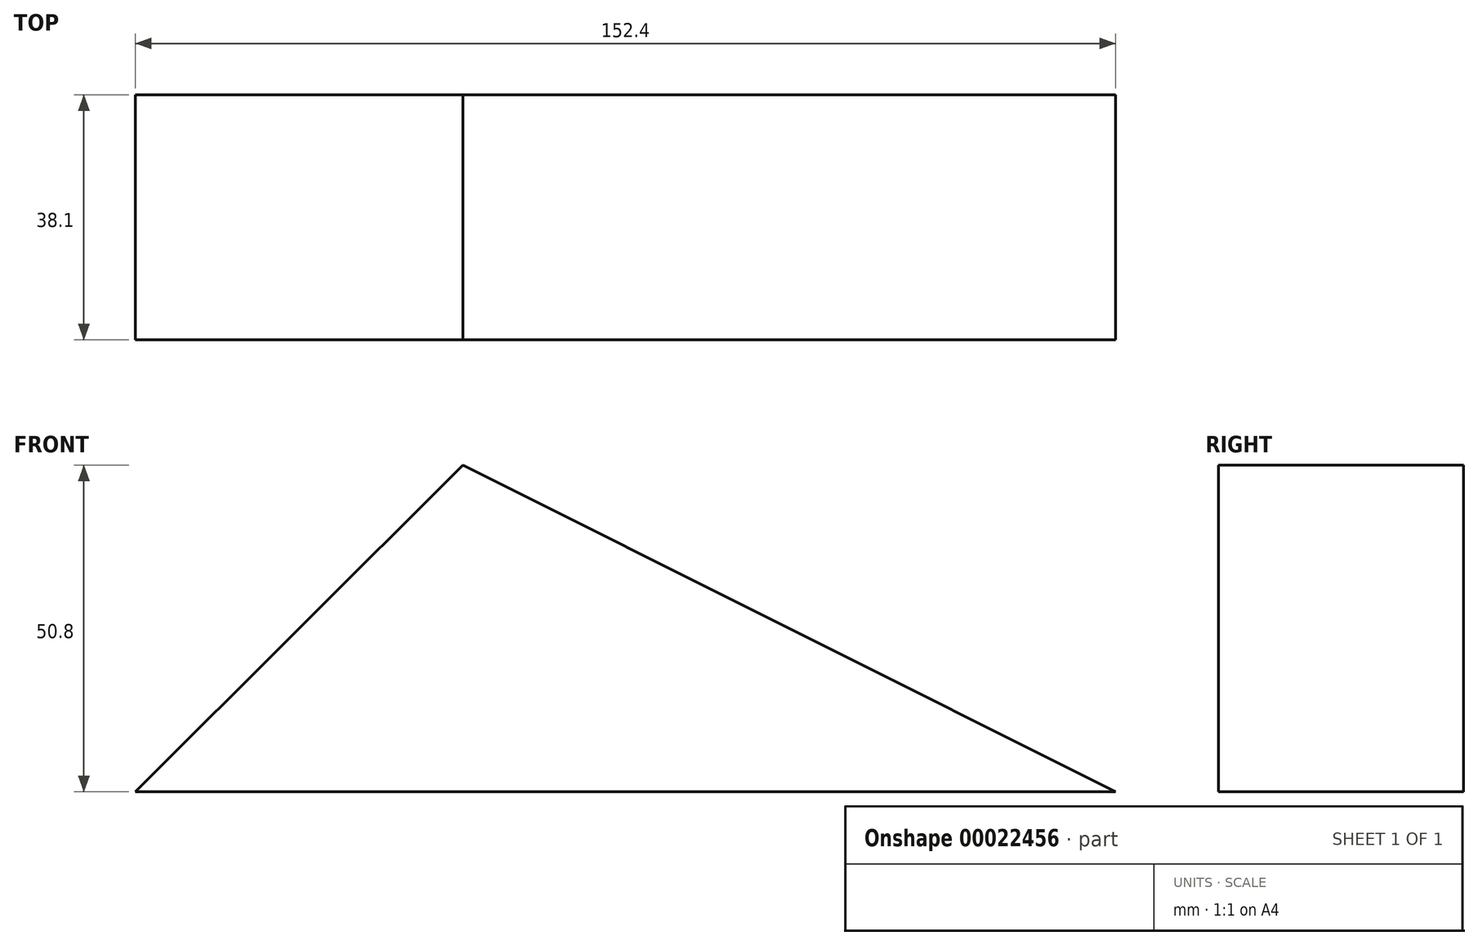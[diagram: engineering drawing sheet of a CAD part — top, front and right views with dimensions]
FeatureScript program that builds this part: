
annotation { "Feature Type Name" : "Feature", "Feature Type Description" : "" }
export const myFeature = defineFeature(function(context is Context, id is Id, definition is map)
    precondition{}
    {
        {
            var Q0;
            Q0=qCreatedBy(makeId("Front.planeOp"),FACE);
            var sketch = newSketch(context, id + "F0", { "sketchPlane" : qUnion([Q0])});
            skLineSegment(sketch, "E0", {"start": v(-50.9, 0) * mm, "end": v(0, 50.8) * mm});
            skLineSegment(sketch, "E1", {"start": v(0, 50.8) * mm, "end": v(101.5, 0) * mm});
            skLineSegment(sketch, "E2", {"start": v(101.5, 0) * mm, "end": v(-50.9, 0) * mm});
            skSolve(sketch);
        }
        {
            var Q0;
            Q0 = qSketchRegion(id + "F0", true);
            extrude(context, id + "F1", {"entities" : qUnion([Q0]), "depth" : 38.1 * mm});
        }
    });
